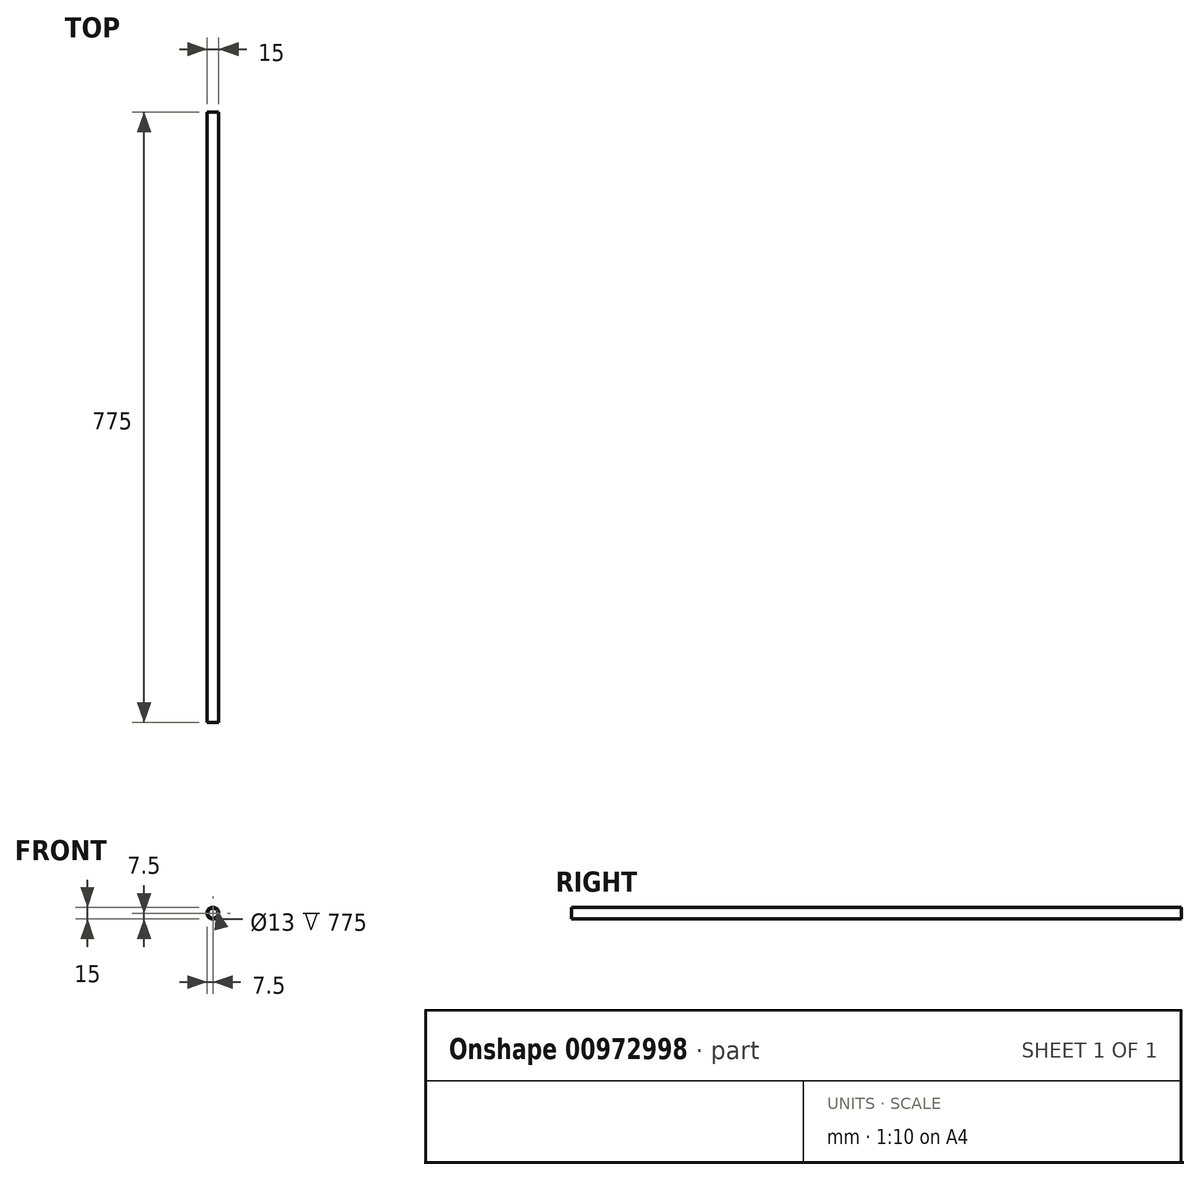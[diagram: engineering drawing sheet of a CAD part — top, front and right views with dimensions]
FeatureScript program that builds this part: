
annotation { "Feature Type Name" : "Feature", "Feature Type Description" : "" }
export const myFeature = defineFeature(function(context is Context, id is Id, definition is map)
    precondition{}
    {
        {
            var Q0;
            Q0=qCreatedBy(makeId("Front.planeOp"),FACE);
            var sketch = newSketch(context, id + "F0", { "sketchPlane" : qUnion([Q0])});
            skCircle(sketch, "E0", {"center": v(0, 0) * mm, "radius": 7.5 * mm});
            skCircle(sketch, "E1", {"center": v(0, 0) * mm, "radius": 6.5 * mm});
            skSolve(sketch);
        }
        {
            var Q0;
            Q0 = qSketchRegion(id + "F0", true);
            extrude(context, id + "F1", {"entities" : qUnion([Q0]), "depth" : 775 * mm, "offsetDistance" : 25 * mm});
        }
    });
